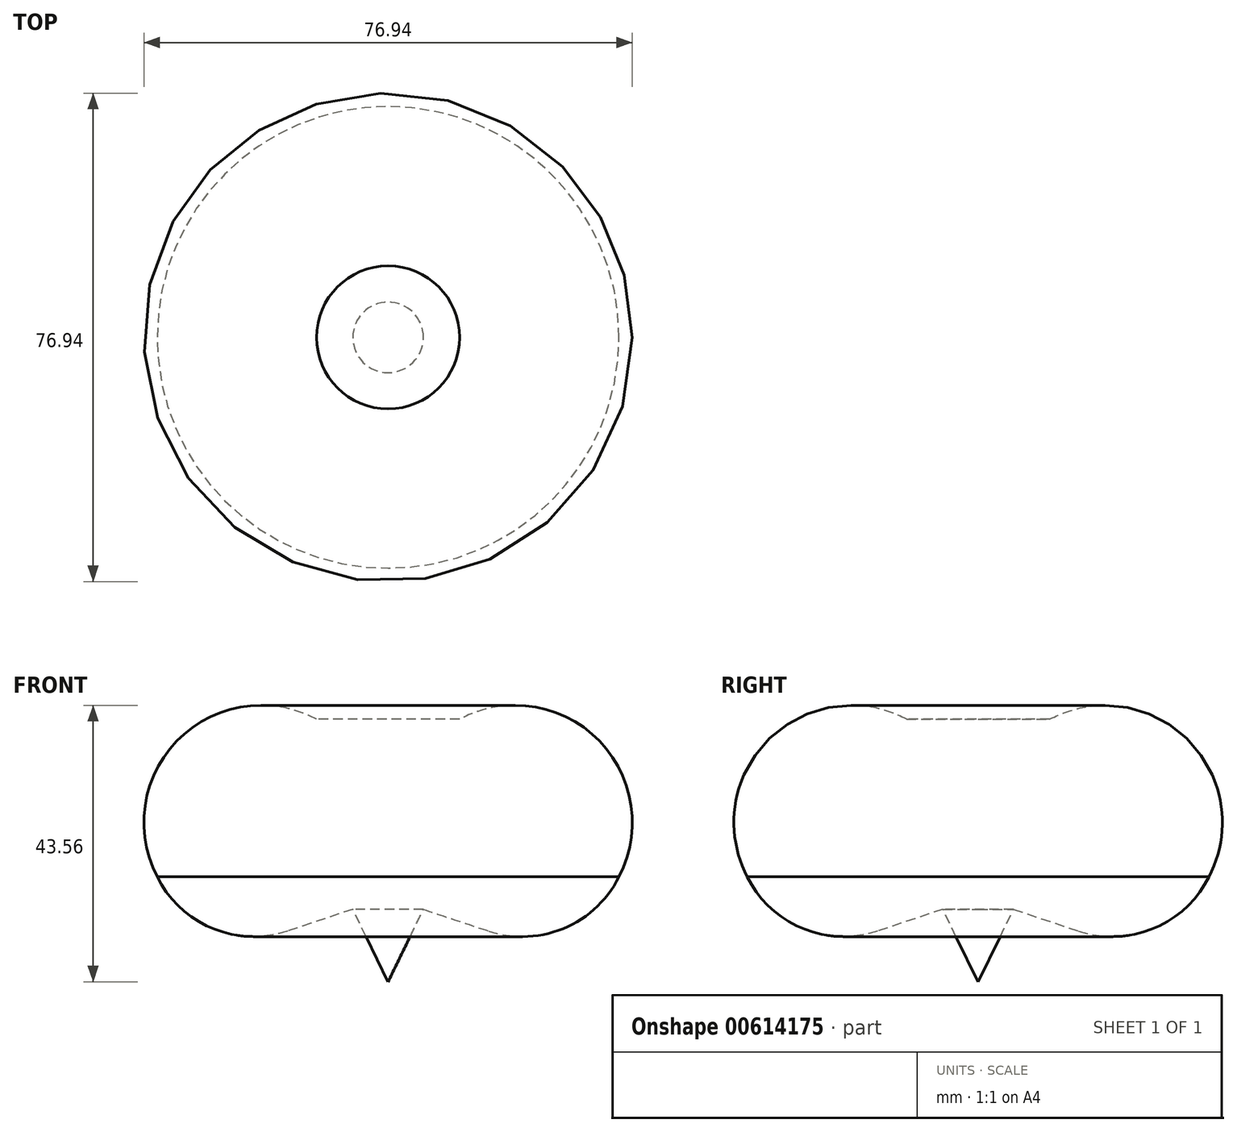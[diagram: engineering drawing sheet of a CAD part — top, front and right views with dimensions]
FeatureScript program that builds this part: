
annotation { "Feature Type Name" : "Feature", "Feature Type Description" : "" }
export const myFeature = defineFeature(function(context is Context, id is Id, definition is map)
    precondition{}
    {
        {
            var Q0;
            Q0=qCreatedBy(makeId("Front.planeOp"),FACE);
            var sketch = newSketch(context, id + "F0", { "sketchPlane" : qUnion([Q0])});
            skLineSegment(sketch, "E0", {"start": v(0, 0) * mm, "end": v(5.56, 11.4) * mm});
            skLineSegment(sketch, "E1", {"start": v(5.56, 11.4) * mm, "end": v(15.83, 7.99) * mm});
            skArc(sketch, "E2", {"start": v(15.83, 7.99) * mm, "mid": v(27.7, 8.42) * mm, "end": v(36.37, 16.54) * mm});
            skArc(sketch, "E3", {"start": v(36.37, 16.54) * mm, "mid": v(32.99, 38.23) * mm, "end": v(11.27, 41.36) * mm});
            skLineSegment(sketch, "E4", {"start": v(11.27, 41.36) * mm, "end": v(0, 41.36) * mm});
            skLineSegment(sketch, "E5", {"start": v(0, 41.36) * mm, "end": v(0, 0) * mm});
            skSolve(sketch);
        }
        {
            var Q0;
            Q0 = qSketchRegion(id + "F0", true);
            var Q1;
            Q1=makeQuery(id+"F0.imprint","IMPRINT",FACE,{"disambiguationData":[TD([[makeQuery(id+"F0.imprint","IMPRINT",EDGE,{"derivedFrom":sQuery(id+"F0.wireOp",EDGE,"E0")}),1.0]])]});
            var Q2;
            Q2=sQuery(id+"F0.wireOp",EDGE,"E5");
            revolve(context, id + "F1", {"entities" : qUnion([Q0, Q1]), "axis" : qUnion([Q2]), "revolveType" : RevolveType.FULL});
        }
    });
